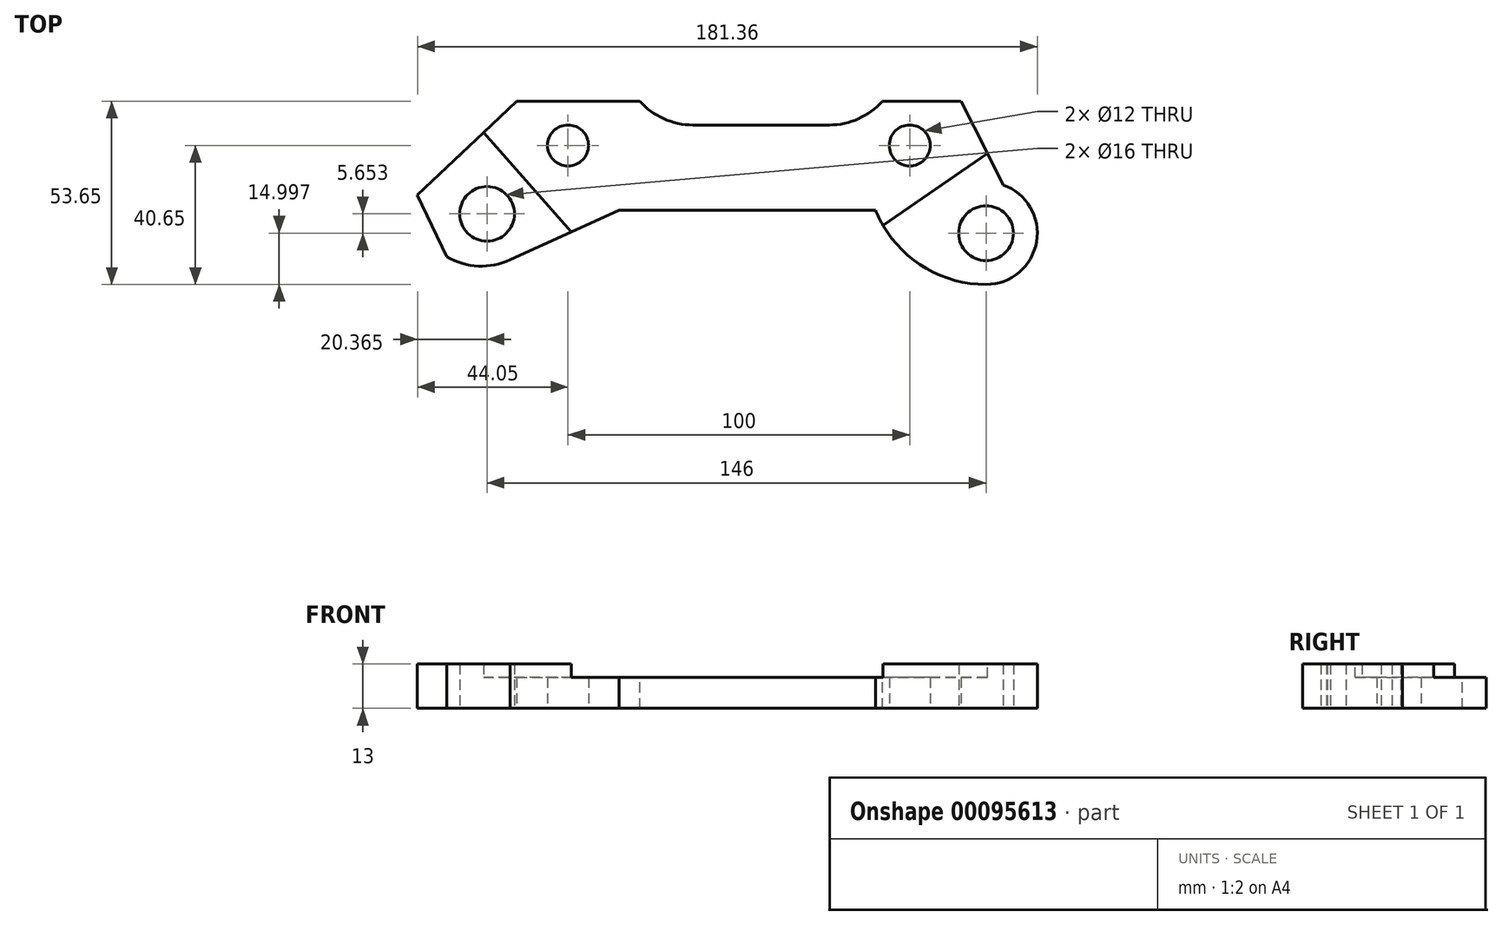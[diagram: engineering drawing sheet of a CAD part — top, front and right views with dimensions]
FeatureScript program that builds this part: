
annotation { "Feature Type Name" : "Feature", "Feature Type Description" : "" }
export const myFeature = defineFeature(function(context is Context, id is Id, definition is map)
    precondition{}
    {
        {
            var Q0;
            Q0=qCreatedBy(makeId("Top.planeOp"),FACE);
            var sketch = newSketch(context, id + "F0", { "sketchPlane" : qUnion([Q0])});
            skCircle(sketch, "E0", {"center": v(-73.69, -20) * mm, "radius": 8 * mm});
            skCircle(sketch, "E1", {"center": v(72.31, -25.65) * mm, "radius": 8 * mm});
            skCircle(sketch, "E2", {"center": v(-50, 0) * mm, "radius": 6 * mm});
            skCircle(sketch, "E3", {"center": v(50, 0) * mm, "radius": 6 * mm});
            skLineSegment(sketch, "E4", {"start": v(-94.05, -14.5) * mm, "end": v(-65, 13) * mm});
            skLineSegment(sketch, "E5", {"start": v(-65, 13) * mm, "end": v(65, 13) * mm});
            skLineSegment(sketch, "E6", {"start": v(40, -19) * mm, "end": v(-35, -19) * mm});
            skArc(sketch, "E7", {"start": v(77.31, -11.51) * mm, "mid": v(87.1, -28.19) * mm, "end": v(72.31, -40.65) * mm});
            skLineSegment(sketch, "E8", {"start": v(65, 13) * mm, "end": v(77.31, -11.51) * mm});
            skArc(sketch, "E9", {"start": v(40, -19) * mm, "mid": v(52.87, -34.74) * mm, "end": v(72.31, -40.65) * mm});
            skLineSegment(sketch, "E10", {"start": v(-35, -19) * mm, "end": v(-66.9, -33.4) * mm});
            skArc(sketch, "E11", {"start": v(-85.43, -32.54) * mm, "mid": v(-76.27, -35.3) * mm, "end": v(-66.9, -33.4) * mm});
            skLineSegment(sketch, "E12", {"start": v(-94.05, -14.5) * mm, "end": v(-85.43, -32.54) * mm});
            skSolve(sketch);
        }
        {
            var Q0;
            Q0=makeQuery(id+"F0.imprint","IMPRINT",FACE,{"disambiguationData":[TD([[makeQuery(id+"F0.imprint","IMPRINT",EDGE,{"derivedFrom":sQuery(id+"F0.wireOp",EDGE,"E0")}),-1.0]])]});
            extrude(context, id + "F1", {"entities" : qUnion([Q0]), "depth" : 13 * mm});
        }
        {
            var Q0;
            Q0=makeQuery(id+"F1.opExtrude","CAP_FACE",FACE,{"disambiguationData":[OSD([sQuery(id+"F0.wireOp",EDGE,"E0"),sQuery(id+"F0.wireOp",EDGE,"E1"),sQuery(id+"F0.wireOp",EDGE,"E2"),sQuery(id+"F0.wireOp",EDGE,"E3"),sQuery(id+"F0.wireOp",EDGE,"E4"),sQuery(id+"F0.wireOp",EDGE,"E5"),sQuery(id+"F0.wireOp",EDGE,"E6"),sQuery(id+"F0.wireOp",EDGE,"E7"),sQuery(id+"F0.wireOp",EDGE,"E8"),sQuery(id+"F0.wireOp",EDGE,"E9"),sQuery(id+"F0.wireOp",EDGE,"E10"),sQuery(id+"F0.wireOp",EDGE,"E11"),sQuery(id+"F0.wireOp",EDGE,"E12")])],"isStart":false});
            var sketch = newSketch(context, id + "F2", { "sketchPlane" : qUnion([Q0])});
            skLineSegment(sketch, "E13", {"start": v(-93.43, 25) * mm, "end": v(112.54, 25) * mm});
            skLineSegment(sketch, "E14", {"start": v(112.54, 25) * mm, "end": v(-15.67, -63) * mm});
            skLineSegment(sketch, "E15", {"start": v(-15.67, -63) * mm, "end": v(-93.43, 25) * mm});
            skSolve(sketch);
        }
        {
            var Q0;
            Q0 = qSketchRegion(id + "F2", true);
            extrude(context, id + "F3", {"entities" : qUnion([Q0]), "operationType" : NewBodyOperationType.REMOVE, "oppositeDirection" : true, "depth" : 4 * mm});
        }
        {
            var Q0;
            Q0=makeQuery(id+"F3.boolean.opBoolean","COPY",FACE,{"derivedFrom":makeQuery(id+"F3.opExtrude","CAP_FACE",FACE,{"disambiguationData":[OSD([sQuery(id+"F2.wireOp",EDGE,"E13"),sQuery(id+"F2.wireOp",EDGE,"E14"),sQuery(id+"F2.wireOp",EDGE,"E15")])],"isStart":false})});
            var sketch = newSketch(context, id + "F4", { "sketchPlane" : qUnion([Q0])});
            skLineSegment(sketch, "E16", {"start": v(-29, 13) * mm, "end": v(42, 13) * mm});
            skLineSegment(sketch, "E17", {"start": v(26.5, 6) * mm, "end": v(-13.5, 6) * mm});
            skPoint(sketch, "E18", {"position": v(-50, 0) * mm});
            skArc(sketch, "E19", {"start": v(-29, 13) * mm, "mid": v(-22, 7.83) * mm, "end": v(-13.5, 6) * mm});
            skArc(sketch, "E20", {"start": v(26.5, 6) * mm, "mid": v(35, 7.83) * mm, "end": v(42, 13) * mm});
            skSolve(sketch);
        }
        {
            var Q0;
            Q0 = qSketchRegion(id + "F4", true);
            extrude(context, id + "F5", {"entities" : qUnion([Q0]), "operationType" : NewBodyOperationType.REMOVE, "endBound" : BoundingType.UP_TO_NEXT, "oppositeDirection" : true, "depth" : 25 * mm});
        }
    });
